# Revit family: Double_-_Double_Hung_-_Grid_-_5_Piece_Trim_6508
name_source: partatom
category: Windows
revit_build: Autodesk Revit LT 2016 (Build: 20150714_1515(x64)
units: mm (PartAtom-declared; Revit-internal decimal feet)

## family parameters
Always vertical = Yes
Cut with Voids When Loaded = No
Host = Wall
Room Calculation Point = No
Shared = No

## types (2) — shared parameters
Analytic Construction = <None>
Default Sill Height = 1' - 10"
Frame Material = Door - Frame
Frame Thickness = 0' - 1"
Grid Thickness = 0' - 0 1/2"
Height = 6' - 0"
Lintel Trim 1 Overhang = 0' - 1"
Lintel Trim 1 Projection = 0' - 1 1/2"
Lintel Trim 1 Width = 0' - 3 1/2"
Lintel Trim 2 Overhang = 0' - 1"
Lintel Trim 2 Projection = 0' - 2 1/2"
Lintel Trim 2 Width = 0' - 1"
Rough Height = 6' - 0 1/2"
Rough Width = 6' - 0 1/2"
Sash Material = Door - Frame
Sash Thickness = 0' - 1 3/4"
Sill Trim Overhang = 0' - 1"
Sill Trim Projection = 0' - 2"
Sill Trim Width = 0' - 2"
Trim Material = Door - Panel
Trim Projection = 0' - 1"
Trim Width = 0' - 3 1/2"
Wall Closure = By host
Width = 6' - 0"

## per-type parameters (varying)
| type | Window Height |
| 72"x60" | 5' - 0" |
| 72"x72" | 6' - 0" |

## geometry (parser evidence)
native form markers: Blend x6, Sweep x9
no freeform markers — native parametric forms only
